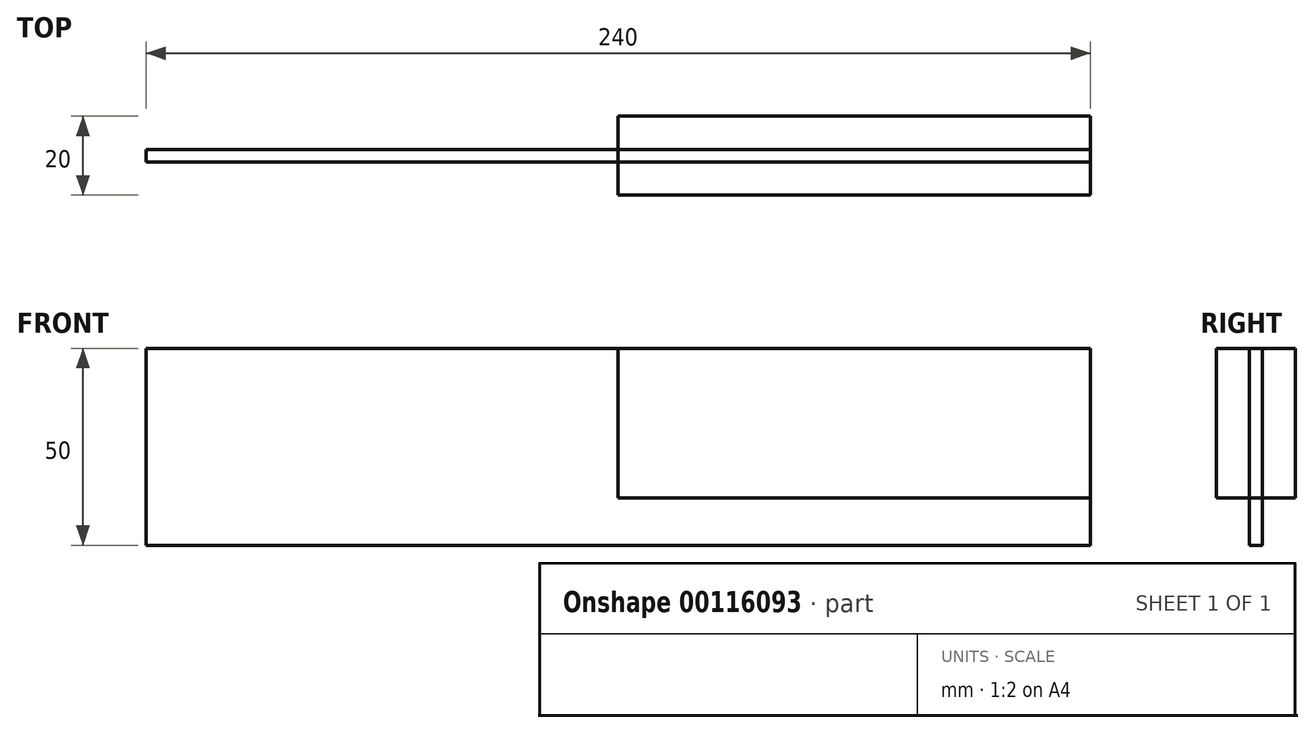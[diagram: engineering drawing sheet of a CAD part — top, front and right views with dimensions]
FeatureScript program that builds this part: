
annotation { "Feature Type Name" : "Feature", "Feature Type Description" : "" }
export const myFeature = defineFeature(function(context is Context, id is Id, definition is map)
    precondition{}
    {
        {
            var Q0;
            Q0=qCreatedBy(makeId("Front.planeOp"),FACE);
            var sketch = newSketch(context, id + "F0", { "sketchPlane" : qUnion([Q0])});
            skLineSegment(sketch, "E0.bottom", {"start": v(0, 0) * mm, "end": v(240, 0) * mm});
            skLineSegment(sketch, "E0.top", {"start": v(0, -50) * mm, "end": v(240, -50) * mm});
            skLineSegment(sketch, "E0.left", {"start": v(0, 0) * mm, "end": v(0, -50) * mm});
            skLineSegment(sketch, "E0.right", {"start": v(240, 0) * mm, "end": v(240, -50) * mm});
            skSolve(sketch);
        }
        {
            var Q0;
            Q0=makeQuery(id+"F0.imprint","IMPRINT",FACE,{"disambiguationData":[TD([[makeQuery(id+"F0.imprint","IMPRINT",EDGE,{"derivedFrom":sQuery(id+"F0.wireOp",EDGE,"E0.bottom")}),-1.0]])]});
            var sketch = newSketch(context, id + "F1", { "sketchPlane" : qUnion([Q0])});
            skLineSegment(sketch, "E1.bottom", {"start": v(120, 0) * mm, "end": v(240, 0) * mm});
            skLineSegment(sketch, "E1.top", {"start": v(120, -38) * mm, "end": v(240, -38) * mm});
            skLineSegment(sketch, "E1.left", {"start": v(120, 0) * mm, "end": v(120, -38) * mm});
            skLineSegment(sketch, "E1.right", {"start": v(240, 0) * mm, "end": v(240, -38) * mm});
            skSolve(sketch);
        }
        {
            var Q0;
            Q0 = qSketchRegion(id + "F0", true);
            extrude(context, id + "F2", {"entities" : qUnion([Q0]), "endBound" : BoundingType.SYMMETRIC, "depth" : 3.2 * mm});
        }
        {
            var Q0;
            Q0 = qSketchRegion(id + "F1", true);
            extrude(context, id + "F3", {"entities" : qUnion([Q0]), "endBound" : BoundingType.SYMMETRIC, "depth" : 20 * mm});
        }
    });
